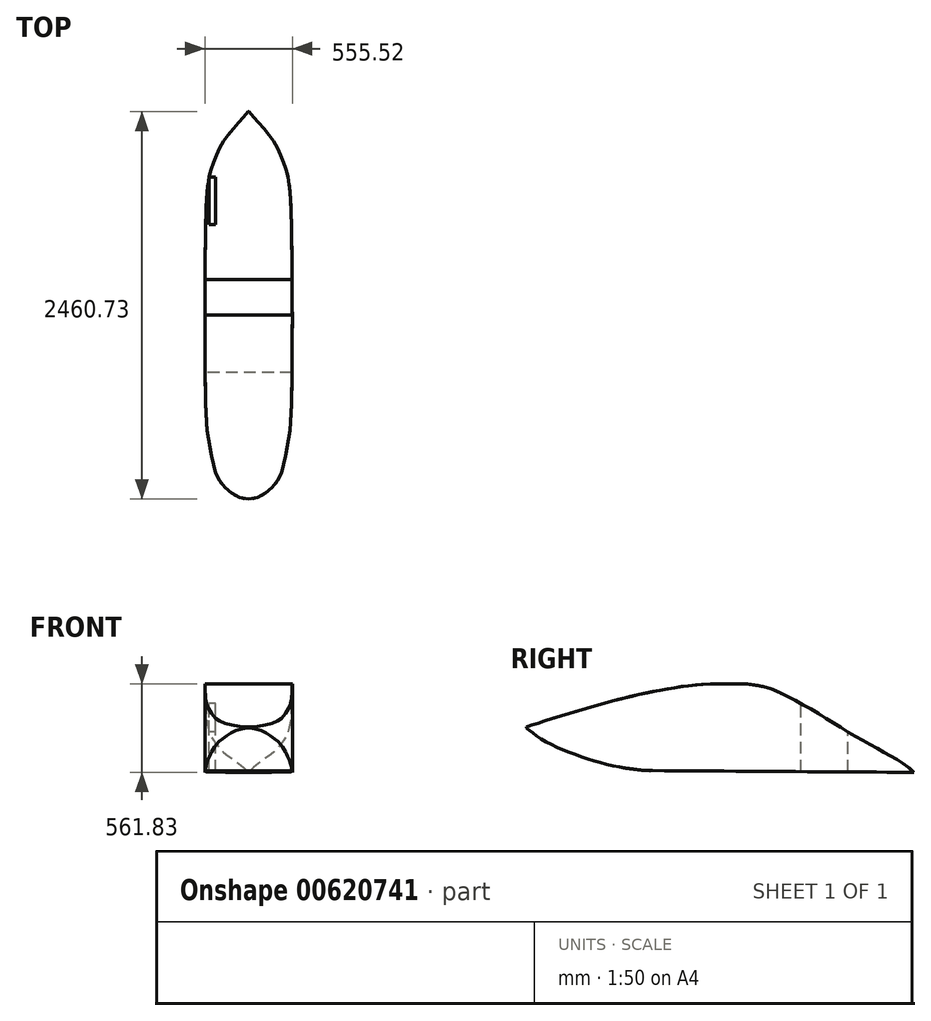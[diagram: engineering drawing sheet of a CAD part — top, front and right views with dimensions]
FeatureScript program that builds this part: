
annotation { "Feature Type Name" : "Feature", "Feature Type Description" : "" }
export const myFeature = defineFeature(function(context is Context, id is Id, definition is map)
    precondition{}
    {
        {
            var Q0;
            Q0=qCreatedBy(makeId("Right.planeOp"),FACE);
            var sketch = newSketch(context, id + "F0", { "sketchPlane" : qUnion([Q0])});
            skFitSpline(sketch, "E0", {"points": [v(-73.35, 286.83) * mm, v(232.82, 383.9) * mm, v(607.34, 485.51) * mm, v(961.53, 550.83) * mm, v(1099.43, 561.83) * mm], "startDerivative": vector(1142.68, 370.23) * mm, "endDerivative": vector(705.94, 34.4) * mm});
            skFitSpline(sketch, "E1", {"points": [v(-73.35, 286.83) * mm, v(31.04, 208.25) * mm, v(196.53, 131.32) * mm, v(472.34, 44.22) * mm, v(695.88, 11.83) * mm, v(733.62, 11.57) * mm], "startDerivative": vector(541.1, -452.38) * mm, "endDerivative": vector(305.7, 14.29) * mm});
            skFitSpline(sketch, "E2", {"points": [v(2392.32, 0) * mm, v(2049.86, 212.3) * mm, v(1772.64, 381.23) * mm, v(1560.66, 496.92) * mm, v(1456.53, 539.22) * mm, v(1324.69, 561.83) * mm], "startDerivative": vector(-372.03, 569) * mm, "endDerivative": vector(-707.7, 78.6) * mm});
            skLineSegment(sketch, "E3", {"start": v(1099.43, 561.83) * mm, "end": v(1324.69, 561.83) * mm});
            skLineSegment(sketch, "E4", {"start": v(733.62, 11.57) * mm, "end": v(2392.32, 0) * mm});
            skLineSegment(sketch, "E5", {"start": v(-73.35, 286.83) * mm, "end": v(-73.35, 561.83) * mm, "construction": true});
            skLineSegment(sketch, "E6", {"start": v(-73.35, 561.83) * mm, "end": v(1099.43, 561.83) * mm, "construction": true});
            skLineSegment(sketch, "E7", {"start": v(1324.69, 561.83) * mm, "end": v(2392.32, 557.83) * mm, "construction": true});
            skLineSegment(sketch, "E8", {"start": v(2392.32, 557.83) * mm, "end": v(2392.32, 0) * mm, "construction": true});
            skSolve(sketch);
        }
        {
            var Q0;
            {var subQ0=sQuery(id+"F0.wireOp",EDGE,"E0");Q0=makeQuery(id+"F0.imprint","IMPRINT",FACE,{"disambiguationData":[TD([[makeQuery(id+"F0.imprint","IMPRINT",EDGE,{"derivedFrom":subQ0}),-1.0]])]});}
            extrude(context, id + "F1", {"entities" : qUnion([Q0]), "endBound" : BoundingType.SYMMETRIC, "depth" : 600 * mm, "offsetDistance" : 25 * mm});
        }
        {
            var Q0;
            Q0=makeQuery(id+"F1.opExtrude","SWEPT_FACE",FACE,{"disambiguationData":[OSD([sQuery(id+"F0.wireOp",EDGE,"E3")])]});
            cPlane(context, id + "F2", {"entities" : qUnion([Q0]), "cplaneType" : CPlaneType.OFFSET, "offset" : 25 * mm, "width" : 150 * mm, "height" : 150 * mm});
        }
        {
            var Q0;
            Q0=qCreatedBy(id+"F2.planeOp",FACE);
            var sketch = newSketch(context, id + "F3", { "sketchPlane" : qUnion([Q0])});
            skLineSegment(sketch, "E9", {"start": v(0, 1748.27) * mm, "end": v(-270, 1748.27) * mm, "construction": true});
            skFitSpline(sketch, "E10", {"points": [v(0, 2394.7) * mm, v(-156.92, 2206.6) * mm, v(-203.07, 2116.08) * mm, v(-240.88, 2017.58) * mm, v(-270, 1744.94) * mm, v(-270, 469.62) * mm, v(-252.28, 300.91) * mm, v(-206.68, 93.46) * mm, v(-145.13, 0) * mm, v(-65.34, -54.73) * mm, v(0, -68.4) * mm], "startDerivative": vector(-1116.02, -1284.3) * mm, "endDerivative": vector(1182.5, -124.78) * mm});
            skFitSpline(sketch, "E11.MirrorCS", {"points": [v(0, 2394.7) * mm, v(156.92, 2206.6) * mm, v(203.07, 2116.08) * mm, v(240.88, 2017.58) * mm, v(270, 1744.94) * mm, v(270, 469.62) * mm, v(252.28, 300.91) * mm, v(206.68, 93.46) * mm, v(145.13, 0) * mm, v(65.34, -54.73) * mm, v(0, -68.4) * mm], "startDerivative": vector(1116.02, -1284.3) * mm, "endDerivative": vector(-1182.5, -124.78) * mm});
            skLineSegment(sketch, "E12.bottom", {"start": v(-959.09, 2925.72) * mm, "end": v(813.99, 2925.72) * mm});
            skLineSegment(sketch, "E12.top", {"start": v(-959.09, -566.2) * mm, "end": v(813.99, -566.2) * mm});
            skLineSegment(sketch, "E12.left", {"start": v(-959.09, 2925.72) * mm, "end": v(-959.09, -566.2) * mm});
            skLineSegment(sketch, "E12.right", {"start": v(813.99, 2925.72) * mm, "end": v(813.99, -566.2) * mm});
            skSolve(sketch);
        }
        {
            var Q0;
            Q0=makeQuery(id+"F3.imprint","IMPRINT",FACE,{"disambiguationData":[TD([[makeQuery(id+"F3.imprint","IMPRINT",EDGE,{"derivedFrom":sQuery(id+"F3.wireOp",EDGE,"E10")}),-1.0]])]});
            extrude(context, id + "F4", {"entities" : qUnion([Q0]), "operationType" : NewBodyOperationType.REMOVE, "oppositeDirection" : true, "depth" : 2850 * mm, "offsetDistance" : 25 * mm});
        }
        {
            var Q0;
            Q0=qCreatedBy(id+"F2.planeOp",FACE);
            var sketch = newSketch(context, id + "F5", { "sketchPlane" : qUnion([Q0])});
            skLineSegment(sketch, "E13.bottom", {"start": v(-250, 1674.69) * mm, "end": v(-210, 1674.69) * mm});
            skLineSegment(sketch, "E13.top", {"start": v(-250, 1974.69) * mm, "end": v(-210, 1974.69) * mm});
            skLineSegment(sketch, "E13.left", {"start": v(-250, 1674.69) * mm, "end": v(-250, 1974.69) * mm});
            skLineSegment(sketch, "E13.right", {"start": v(-210, 1674.69) * mm, "end": v(-210, 1974.69) * mm});
            skLineSegment(sketch, "E14.MirrorCS", {"start": v(210, 1674.69) * mm, "end": v(210, 1974.69) * mm});
            skLineSegment(sketch, "E15.MirrorCS", {"start": v(250, 1974.69) * mm, "end": v(210, 1974.69) * mm});
            skLineSegment(sketch, "E16.MirrorCS", {"start": v(250, 1674.69) * mm, "end": v(250, 1974.69) * mm});
            skLineSegment(sketch, "E17.MirrorCS", {"start": v(250, 1674.69) * mm, "end": v(210, 1674.69) * mm});
            skLineSegment(sketch, "E18", {"start": v(-210, 1824.69) * mm, "end": v(-250, 1824.69) * mm, "construction": true});
            skLineSegment(sketch, "E19", {"start": v(210, 1824.69) * mm, "end": v(250, 1824.69) * mm, "construction": true});
            skSolve(sketch);
        }
        {
            var Q0;
            Q0=makeQuery(id+"F5.imprint","IMPRINT",FACE,{"disambiguationData":[TD([[makeQuery(id+"F5.imprint","IMPRINT",EDGE,{"derivedFrom":sQuery(id+"F5.wireOp",EDGE,"E13.bottom")}),1.0]])]});
            extrude(context, id + "F6", {"entities" : qUnion([Q0]), "operationType" : NewBodyOperationType.REMOVE, "oppositeDirection" : true, "depth" : 761 * mm, "offsetDistance" : 25 * mm});
        }
    });
